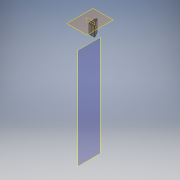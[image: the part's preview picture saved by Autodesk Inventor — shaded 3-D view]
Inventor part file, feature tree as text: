
AUTODESK INVENTOR PART (.ipt)
format: ipt  version: 2018 (Build 220112000, 112)  size: 454,656 bytes
history: native  units: mm
features: sheet_metal_op x8, other x7, plane x4, sketch x4, reference x3, extrude x1, projected_geometry x1
ambient origin geometry x8: Origin, YZ Plane, XZ Plane, XY Plane, X Axis, Y Axis, Z Axis, Center Point
bodies: Body1 (feature_tree)
feature tree (28):
  plane  "Work Plane1"
  plane  "Work Plane3"
  sheet_metal_op  "Contour Flange2"
  sheet_metal_op  "Flange1"
  plane  "Work Plane4"
  extrude  "Extrusion1"  Depth=10.0mm
  sheet_metal_op  "Unfold1"
  sheet_metal_op  "Refold1"
  sketch  "Sketch1"  dims[d12=10.0mm d13=10.0mm]
  reference  "Reference1"
  reference  "Reference2"
  reference  "Reference3"
  plane  "Work Plane2"
  other  "Plate2"
  sheet_metal_op  "Bend2"
  sheet_metal_op  "Corner2"
  sketch  "Sketch3"  dims[d14=2.0mm]
  other  "Plate3"
  sheet_metal_op  "Bend3"
  sheet_metal_op  "Corner3"
  sketch  "Sketch4"  dims[d15=2.0mm]
  sketch  "Sketch5"  dims[d16=1.0mm d17=4.0mm d18=2.0mm d19=200.0mm d20=2.0mm d21=2.0mm d22=8.0mm d23=2.0mm d24=2.0mm d25=2.0mm d26=1.0mm d27=4.0mm d28=2.0mm d29=33.477mm d30=20.628046mm d31=2.0mm d32=8.0mm d33=2.0mm d34=2.0mm d37=10.0mm d38=0.0mm d39=5.674267mm d40=2.837133mm d41=6.0mm d42=21.0mm d43=5.5mm d44=70.0mm d46=26.5mm d47=10.0mm d49=10.0mm d51=2.0mm d52=0.0mm d53=5.986479mm d54=10.0mm d55=5.5mm]
  projected_geometry  "Projected Loop1"
  other  "Cut1"
  parser-record x1  (decoder bookkeeping rows leaked as tree rows — omitted from the tree; the rows remain in map.json)
  other  "svejselære.iam"
  other  "plade:1"
  other  "Definition1"
note: 1 file-system path scrubbed to <path> (originals preserved in map.json)
